# Revit family: Seal_Trap_Barrier-Zurn-Z1072
name_source: partatom
category: Plumbing Fixtures
units: mm (PartAtom-declared; Revit-internal decimal feet)

## family parameters
Always vertical = Yes
Cut with Voids When Loaded = No
Maintain Annotation Orientation = No
OmniClass Number = 23.45.55.21
OmniClass Title = Drains (Wastes)
Part Type = Normal
Room Calculation Point = No
Round Connector Dimension = Use Radius
Shared = No
Work Plane-Based = No

## types (4) — shared parameters
Assembly Code = D2030100
CW Connection = No
Default Elevation = 20 "
Description = ZShield™ BARRIER TRAP SEAL DEVICE FOR FLOOR DRAINS
HW Connection = No
Main Material = ABS - Zurn - Acrylonitrile Butadiene Styrene - Black
Manufacturer = Zurn Water, LLC
Manufacturer Brand = Zurn
Model = Z1072
Modified Date = 02/13/2026
Product Documentation Link = https://files.zurn.com
Product Installation Sheet URL = https://files.zurn.com
Product Page URL = https://www.zurn.com
URL = http://zurn.com
Vent Connection = No
WFU = 1
Waste Connection = Yes
zero-valued in all types: CWFU, HWFU

## per-type parameters (varying)
| type | Bottom Diameter | Diameter (A) | Flow Rate (G.P.M.) | Height (B) | Inside Ribs Height | Product data url | Ribs Diameter | Ribs Gap Diameter | Ribs Gap Radius | Tip Thickness |
| Z1072-2 for 2 Inch Pipe/Outlet | 1.672 " | 2.2 " | 12 " | 1.22 " | 0.542 " | https://bimobject.com | 2.075 " | 1.7 " | 0.85 " | 0.07 " |
| Z1072-3 for 3 Inch Pipe/Outlet | 2.5 " | 3.25 " | 34 " | 1.25 " | 0.556 " | https://www.bimobject.com | 3.125 " | 2.75 " | 1.375 " | 0.1 " |
| Z1072-3.5 for 3.5 Inch Pipe/Outlet | 3.15 " | 3.53 " | 52 " | 1.3 " | 0.578 " | https://www.bimobject.com | 3.405 " | 3.03 " | 1.515 " | 0.1 " |
| Z1072-4 for 4 Inch Pipe/Outlet | 3.55 " | 4.13 " | 73 " | 1.3 " | 0.578 " | https://www.bimobject.com | 4.005 " | 3.63 " | 1.815 " | 0.13 " |

## geometry (parser evidence)
native form markers: Sweep x3
no freeform markers — native parametric forms only
